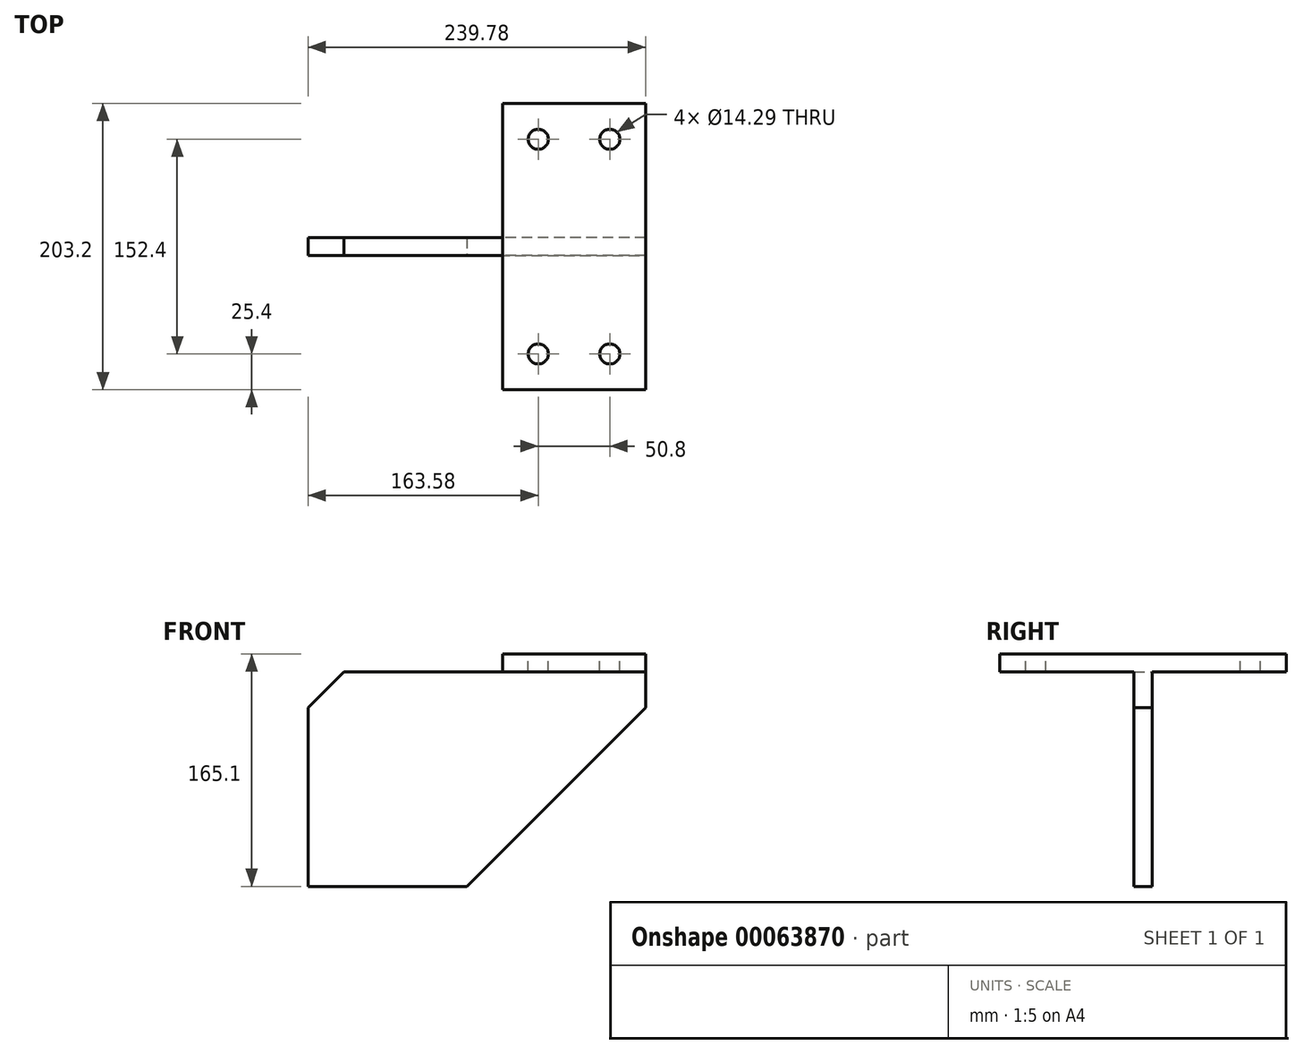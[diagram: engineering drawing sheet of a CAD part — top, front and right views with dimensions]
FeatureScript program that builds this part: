
annotation { "Feature Type Name" : "Feature", "Feature Type Description" : "" }
export const myFeature = defineFeature(function(context is Context, id is Id, definition is map)
    precondition{}
    {
        {
            var Q0;
            Q0=qCreatedBy(makeId("Front.planeOp"),FACE);
            var sketch = newSketch(context, id + "F0", { "sketchPlane" : qUnion([Q0])});
            skLineSegment(sketch, "E0.bottom", {"start": v(0, 0) * mm, "end": v(101.6, 0) * mm});
            skLineSegment(sketch, "E0.top", {"start": v(0, 12.7) * mm, "end": v(101.6, 12.7) * mm});
            skLineSegment(sketch, "E0.left", {"start": v(0, 0) * mm, "end": v(0, 12.7) * mm});
            skLineSegment(sketch, "E0.right", {"start": v(101.6, 0) * mm, "end": v(101.6, 12.7) * mm});
            skSolve(sketch);
        }
        {
            var Q0;
            Q0 = qSketchRegion(id + "F0", true);
            extrude(context, id + "F1", {"entities" : qUnion([Q0]), "endBound" : BoundingType.SYMMETRIC, "depth" : 203.2 * mm});
        }
        {
            var Q0;
            Q0=makeQuery(id+"F1.opExtrude","SWEPT_FACE",FACE,{"disambiguationData":[OSD([sQuery(id+"F0.wireOp",EDGE,"E0.top")])]});
            var sketch = newSketch(context, id + "F2", { "sketchPlane" : qUnion([Q0])});
            skLineSegment(sketch, "E1", {"start": v(101.6, 0) * mm, "end": v(0, 0) * mm, "construction": true});
            skLineSegment(sketch, "E2", {"start": v(50.8, 101.6) * mm, "end": v(50.8, -101.6) * mm, "construction": true});
            skLineSegment(sketch, "E3.0", {"start": v(25.4, 101.6) * mm, "end": v(25.4, -101.6) * mm, "construction": true});
            skLineSegment(sketch, "E4.0", {"start": v(101.6, -76.2) * mm, "end": v(0, -76.2) * mm, "construction": true});
            skPoint(sketch, "E5", {"position": v(25.4, -76.2) * mm});
            skPoint(sketch, "E6.MirrorP", {"position": v(76.2, -76.2) * mm});
            skPoint(sketch, "E7.MirrorP", {"position": v(25.4, 76.2) * mm});
            skPoint(sketch, "E8.MirrorP", {"position": v(76.2, 76.2) * mm});
            skSolve(sketch);
        }
        {
            var Q0;
            Q0=sQuery(id+"F2.wireOp",VERTEX,"E5");
            var Q1;
            Q1=sQuery(id+"F2.wireOp",VERTEX,"E6.MirrorP");
            var Q2;
            Q2=sQuery(id+"F2.wireOp",VERTEX,"E8.MirrorP");
            var Q3;
            Q3=sQuery(id+"F2.wireOp",VERTEX,"E7.MirrorP");
            var Q4;
            Q4=makeQuery(id+"F1.opExtrude","SWEPT_BODY",BODY,{"disambiguationData":[OSD([sQuery(id+"F0.wireOp",EDGE,"E0.bottom"),sQuery(id+"F0.wireOp",EDGE,"E0.top"),sQuery(id+"F0.wireOp",EDGE,"E0.left"),sQuery(id+"F0.wireOp",EDGE,"E0.right")])]});
            hole(context, id + "F3", {"style" : HoleStyle.SIMPLE, "holeDiameter" : 14.29 * mm, "endStyle" : HoleEndStyle.THROUGH, "locations" : qUnion([Q0, Q1, Q2, Q3]), "scope" : qUnion([Q4])});
        }
        {
            var Q0;
            Q0=qCreatedBy(makeId("Front.planeOp"),FACE);
            var sketch = newSketch(context, id + "F4", { "sketchPlane" : qUnion([Q0])});
            skLineSegment(sketch, "E9.0", {"start": v(0, 0) * mm, "end": v(101.6, 0) * mm, "construction": true});
            skLineSegment(sketch, "E10.bottom", {"start": v(101.6, 0) * mm, "end": v(-138.18, 0) * mm});
            skLineSegment(sketch, "E10.top", {"start": v(101.6, -152.4) * mm, "end": v(-138.18, -152.4) * mm});
            skLineSegment(sketch, "E10.left", {"start": v(101.6, 0) * mm, "end": v(101.6, -152.4) * mm});
            skLineSegment(sketch, "E10.right", {"start": v(-138.18, 0) * mm, "end": v(-138.18, -152.4) * mm});
            skSolve(sketch);
        }
        {
            var Q0;
            Q0 = qSketchRegion(id + "F4", true);
            extrude(context, id + "F5", {"entities" : qUnion([Q0]), "operationType" : NewBodyOperationType.ADD, "endBound" : BoundingType.SYMMETRIC, "depth" : 12.7 * mm});
        }
        {
            var Q0;
            Q0=makeQuery(id+"F5.opExtrude","SWEPT_EDGE",EDGE,{"disambiguationData":[OSD([sQuery(id+"F4.wireOp",EDGE,"E10.bottom"),sQuery(id+"F4.wireOp",EDGE,"E10.right")])]});
            chamfer(context, id + "F6", {"entities" : qUnion([Q0]), "width" : 25.4 * mm, "tangentPropagation" : true});
        }
        {
            var Q0;
            Q0=makeQuery(id+"F5.opExtrude","SWEPT_EDGE",EDGE,{"disambiguationData":[OSD([sQuery(id+"F4.wireOp",EDGE,"E10.top"),sQuery(id+"F4.wireOp",EDGE,"E10.left")])]});
            chamfer(context, id + "F7", {"entities" : qUnion([Q0]), "width" : 127 * mm, "tangentPropagation" : true});
        }
    });
